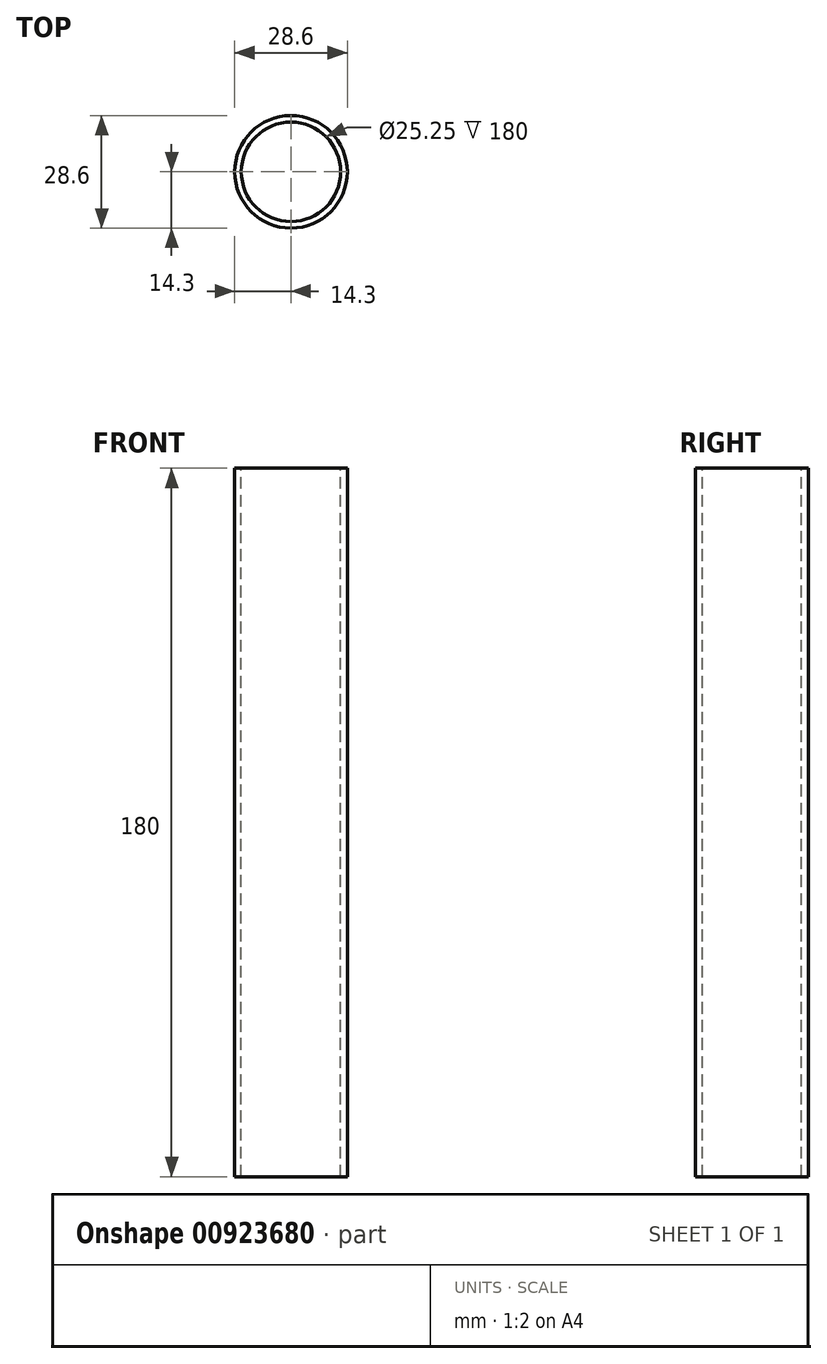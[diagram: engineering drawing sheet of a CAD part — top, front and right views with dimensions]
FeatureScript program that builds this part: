
annotation { "Feature Type Name" : "Feature", "Feature Type Description" : "" }
export const myFeature = defineFeature(function(context is Context, id is Id, definition is map)
    precondition{}
    {
        {
            var Q0;
            Q0=qCreatedBy(makeId("Top.planeOp"),FACE);
            var sketch = newSketch(context, id + "F0", { "sketchPlane" : qUnion([Q0])});
            skCircle(sketch, "E0", {"center": v(0, 0) * mm, "radius": 14.3 * mm});
            skSolve(sketch);
        }
        {
            var Q0;
            Q0=qSketchRegion(id+"F0",true);
            extrude(context, id + "F1", {"entities" : qUnion([Q0]), "depth" : 150 * mm, "offsetDistance" : 25 * mm, "hasSecondDirection" : true, "secondDirectionOppositeDirection" : true, "secondDirectionDepth" : 30 * mm});
        }
        {
            var Q0;
            Q0=makeQuery(id+"F1.opExtrude","CAP_FACE",FACE,{"disambiguationData":[OSD([sQuery(id+"F0.wireOp",EDGE,"E0")])],"isStart":false});
            var sketch = newSketch(context, id + "F2", { "sketchPlane" : qUnion([Q0])});
            skCircle(sketch, "E1", {"center": v(0, 0) * mm, "radius": 12.62 * mm});
            skLineSegment(sketch, "E2", {"start": v(12.62, 0) * mm, "end": v(14.3, 0) * mm, "construction": true});
            skSolve(sketch);
        }
        {
            var Q0;
            Q0=makeQuery(id+"F2.imprint","IMPRINT",FACE,{"disambiguationData":[TD([[makeQuery(id+"F2.imprint","IMPRINT",EDGE,{"derivedFrom":sQuery(id+"F2.wireOp",EDGE,"E1")}),1.0]])]});
            extrude(context, id + "F3", {"entities" : qUnion([Q0]), "operationType" : NewBodyOperationType.REMOVE, "endBound" : BoundingType.THROUGH_ALL, "oppositeDirection" : true, "depth" : 25 * mm, "offsetDistance" : 25 * mm});
        }
    });
